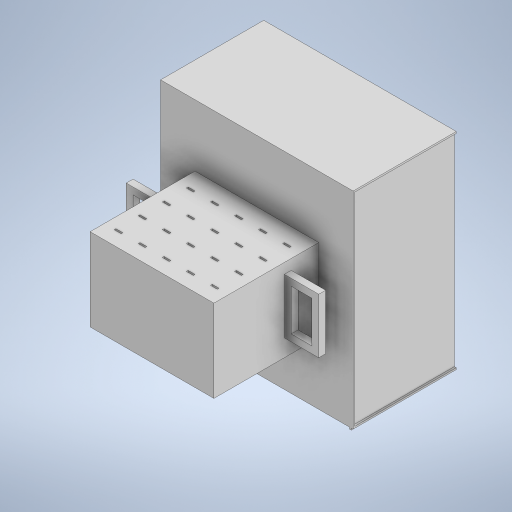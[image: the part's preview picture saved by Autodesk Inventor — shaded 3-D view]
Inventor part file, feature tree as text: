
AUTODESK INVENTOR PART (.ipt)
format: ipt  version: 2024.3 (Build 283343000, 343)  size: 524,288 bytes
history: native  units: mm
features: extrude x14, sketch x14, projected_geometry x3, other x1
ambient origin geometry x8: Origin, YZ Plane, XZ Plane, XY Plane, X Axis, Y Axis, Z Axis, Center Point
bodies: Body1 (feature_tree)
feature tree (32):
  other  "ソリッド1"
  extrude  "押し出し1"  Depth=350.0mm
  extrude  "押し出し2"  Depth=230.0mm
  extrude  "押し出し3"  Depth=5.0mm
  extrude  "押し出し4"  Depth=300.0mm TaperAngle=0.0deg
  extrude  "押し出し5"  Depth=600.0mm
  extrude  "押し出し6"  Depth=300.0mm
  extrude  "押し出し7"  Depth=360.0mm
  extrude  "押し出し8"  Depth=300.0mm TaperAngle=0.0deg
  extrude  "押し出し9"  Depth=4.999988mm
  extrude  "押し出し10"  Depth=295.0mm TaperAngle=0.0deg
  extrude  "押し出し11"  Depth=295.0mm TaperAngle=0.0deg
  extrude  "押し出し12"  Depth=30.0mm
  extrude  "押し出し13"  Depth=30.0mm
  extrude  "押し出し14"  Depth=20.0mm
  sketch  "スケッチ1"
  sketch  "スケッチ2"
  sketch  "スケッチ3"
  projected_geometry  "投影ループ1"
  sketch  "スケッチ4"
  sketch  "スケッチ5"
  sketch  "スケッチ6"
  projected_geometry  "投影ループ2"
  sketch  "スケッチ8"
  sketch  "スケッチ9"
  projected_geometry  "投影ループ3"
  sketch  "スケッチ10"
  sketch  "スケッチ11"
  sketch  "スケッチ12"
  sketch  "スケッチ13"
  sketch  "スケッチ14"
  sketch  "スケッチ15"
